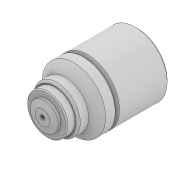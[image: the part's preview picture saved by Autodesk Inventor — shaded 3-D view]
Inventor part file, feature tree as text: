
AUTODESK INVENTOR PART (.ipt)
format: ipt  version: 2020 (Build 240168000, 168)  size: 168,960 bytes
history: native  units: mm
features: sketch x10, extrude x9, chamfer x5, revolve x1
ambient origin geometry x8: Origin, YZ Plane, XZ Plane, XY Plane, X Axis, Y Axis, Z Axis, Center Point
bodies: Solid1 (feature_tree)
feature tree (25):
  extrude  "Extrusion1"  Depth=24.5mm TaperAngle=0.0deg
  chamfer  "Chamfer1"  Distance=1.0mm Angle=45.0deg
  extrude  "Extrusion2"  Depth=2.0mm TaperAngle=0.0deg
  chamfer  "Chamfer2"  Distance=1.0mm Angle=45.0deg
  extrude  "Extrusion3"  Depth=2.0mm TaperAngle=0.0deg
  chamfer  "Chamfer3"  Distance=2.0mm Angle=45.0deg
  extrude  "Extrusion4"  Depth=5.0mm TaperAngle=0.0deg
  extrude  "Extrusion5"  Depth=3.8mm TaperAngle=0.0deg
  chamfer  "Chamfer4"  Distance=1.0mm Angle=45.0deg
  extrude  "Extrusion6"  Depth=0.75mm TaperAngle=0.0deg
  extrude  "Extrusion7"  Depth=1.25mm TaperAngle=0.0deg
  revolve  "Revolution1"  Angle=90.0deg
  extrude  "Extrusion8"  Depth=2.0mm TaperAngle=0.0deg
  extrude  "Extrusion9"  Depth=20.0mm TaperAngle=0.0deg
  chamfer  "Chamfer5"  Distance=0.5mm Angle=45.0deg
  sketch  "Sketch1"  dims[d0=30.0mm d1=24.5mm d2=0.0mm d3=1.0mm d4=2.0mm d5=45.0deg]
  sketch  "Sketch2"  dims[d6=30.0mm d7=5.5mm d8=0.0mm d9=1.0mm d10=2.0mm d11=45.0deg]
  sketch  "Sketch3"  dims[d12=22.0mm d13=4.0mm d14=0.0mm d15=4.0mm d16=2.0mm d17=45.0deg]
  sketch  "Sketch4"  dims[d18=22.0mm d19=5.0mm d20=0.0mm]
  sketch  "Sketch5"  dims[d21=19.0mm d22=3.8mm d23=0.0mm d24=1.0mm d25=2.0mm d26=45.0deg]
  sketch  "Sketch6"  dims[d27=13.2mm d28=0.75mm d29=0.0mm]
  sketch  "Sketch7"  dims[d30=7.1mm d31=1.25mm d32=0.0mm]
  sketch  "Sketch8"  dims[d33=2.527237mm d34=90.0deg]
  sketch  "Sketch9"  dims[d35=2.0mm d36=50.0mm d37=0.0mm]
  sketch  "Sketch10"  dims[d38=4.0mm d39=20.0mm d40=0.0mm d41=0.5mm d42=2.0mm d43=45.0deg]
